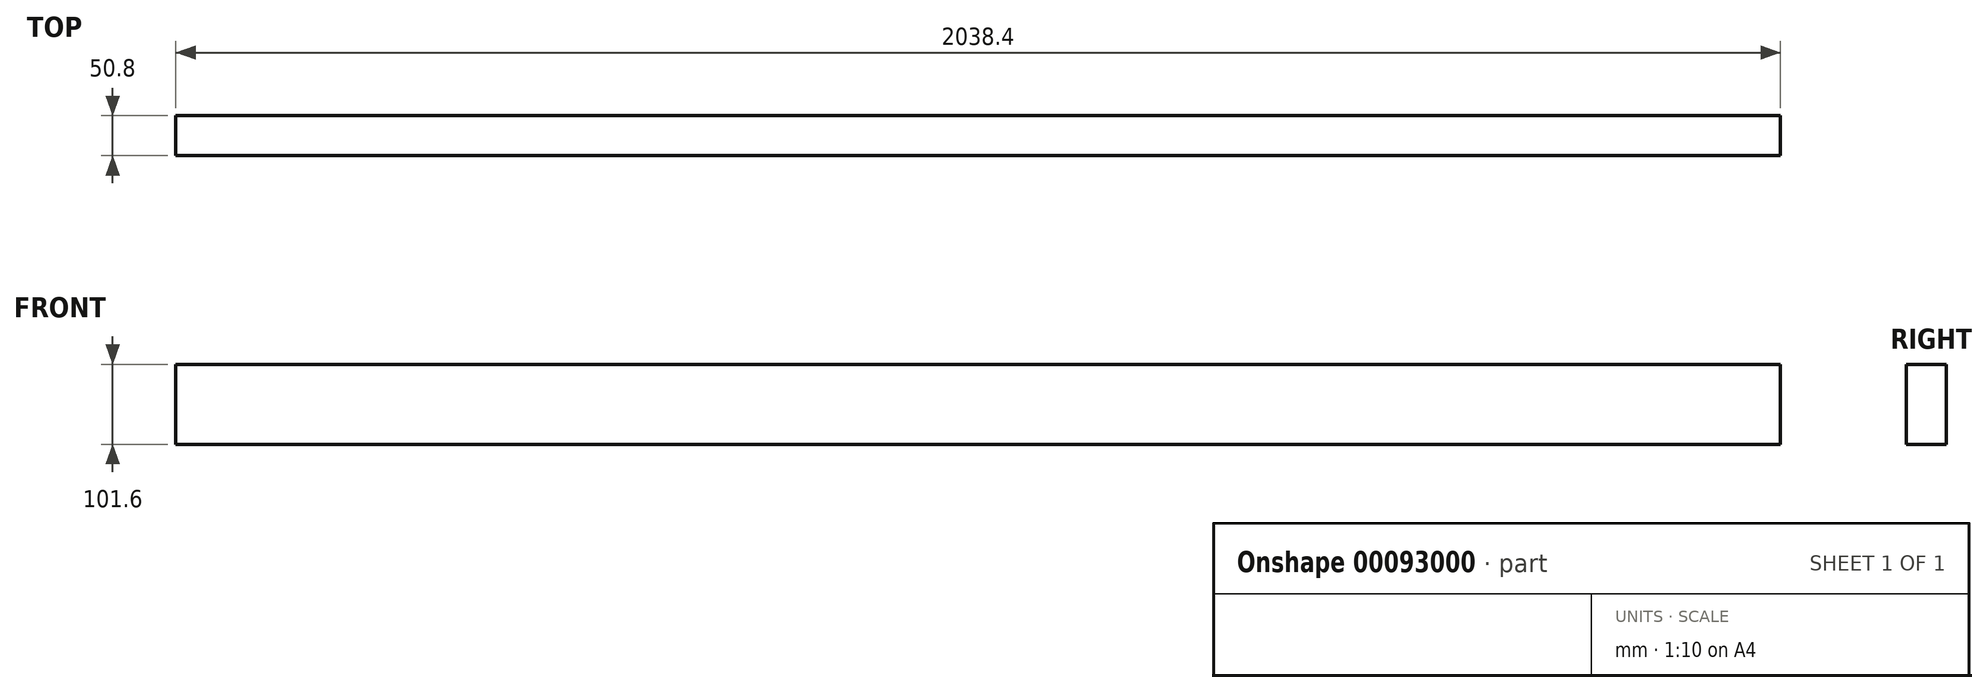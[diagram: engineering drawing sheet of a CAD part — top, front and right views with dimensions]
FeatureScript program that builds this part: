
annotation { "Feature Type Name" : "Feature", "Feature Type Description" : "" }
export const myFeature = defineFeature(function(context is Context, id is Id, definition is map)
    precondition{}
    {
        {
            var Q0;
            Q0=qCreatedBy(makeId("Top.planeOp"),FACE);
            var sketch = newSketch(context, id + "F0", { "sketchPlane" : qUnion([Q0])});
            skLineSegment(sketch, "E0.bottom", {"start": v(-1019.2, 25.4) * mm, "end": v(1019.2, 25.4) * mm});
            skLineSegment(sketch, "E0.top", {"start": v(-1019.2, -25.4) * mm, "end": v(1019.2, -25.4) * mm});
            skLineSegment(sketch, "E1", {"start": v(-1019.2, -25.4) * mm, "end": v(-1019.2, 25.4) * mm});
            skLineSegment(sketch, "E2", {"start": v(1019.2, -25.4) * mm, "end": v(1019.2, 25.4) * mm});
            skSolve(sketch);
        }
        {
            var Q0;
            Q0=qSketchRegion(id+"F0",true);
            extrude(context, id + "F1", {"entities" : qUnion([Q0]), "oppositeDirection" : true, "depth" : 101.6 * mm});
        }
    });
